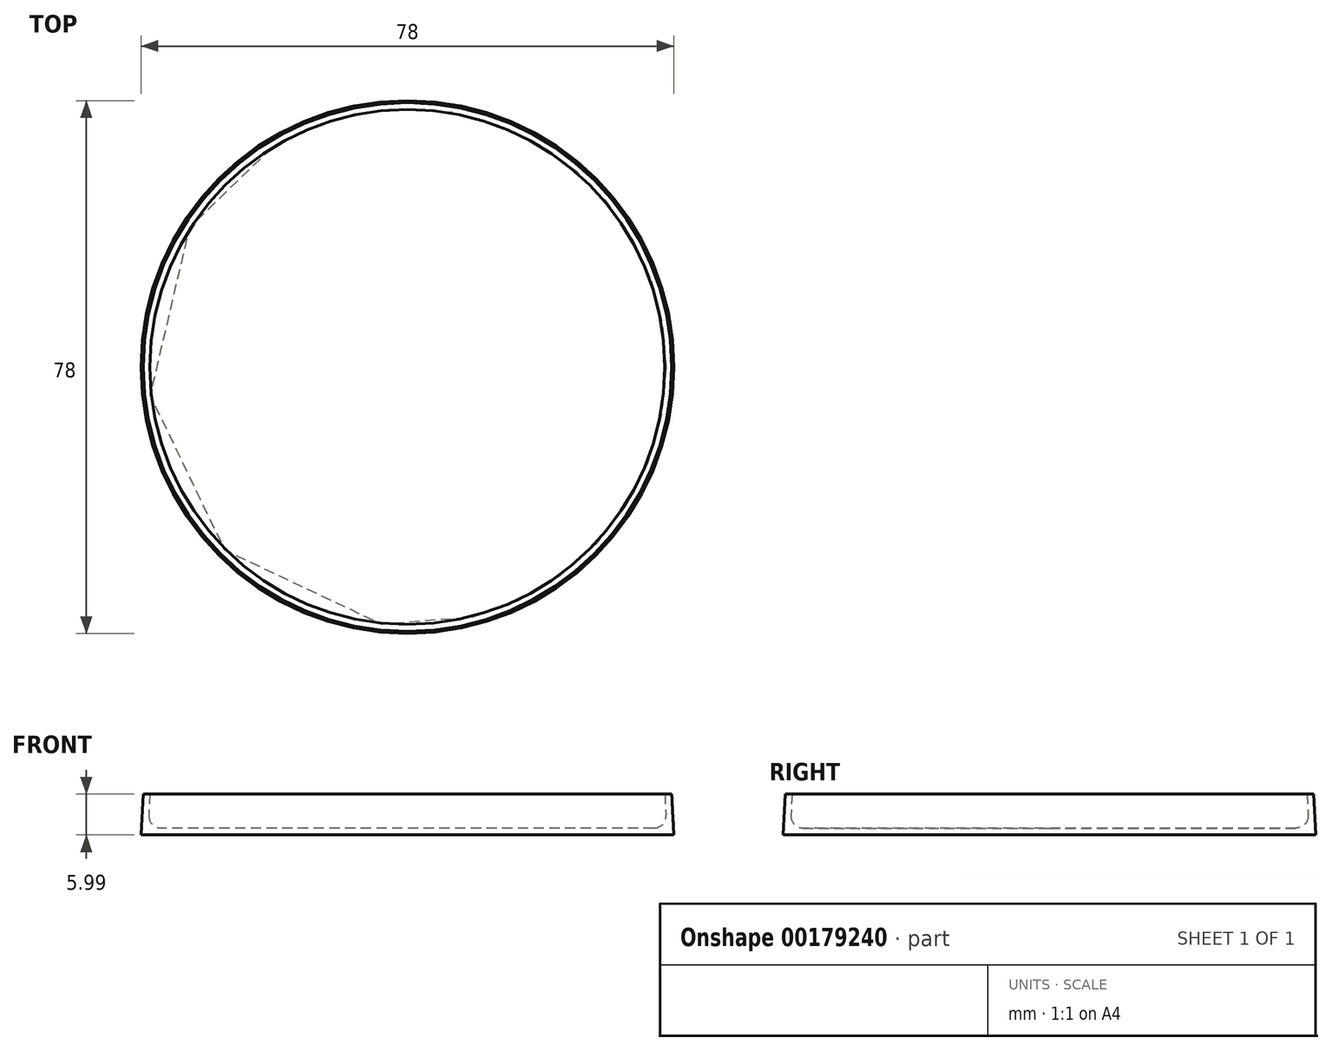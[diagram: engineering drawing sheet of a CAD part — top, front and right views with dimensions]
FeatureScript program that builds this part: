
annotation { "Feature Type Name" : "Feature", "Feature Type Description" : "" }
export const myFeature = defineFeature(function(context is Context, id is Id, definition is map)
    precondition{}
    {
        {
            var Q0;
            Q0=qCreatedBy(makeId("Front.planeOp"),FACE);
            var sketch = newSketch(context, id + "F0", { "sketchPlane" : qUnion([Q0])});
            skLineSegment(sketch, "E0", {"start": v(-39, 0) * mm, "end": v(-38.69, 6) * mm});
            skLineSegment(sketch, "E1", {"start": v(-38.69, 6) * mm, "end": v(-37.69, 6) * mm});
            skLineSegment(sketch, "E2", {"start": v(-37.69, 6) * mm, "end": v(-37.85, 2.87) * mm});
            skLineSegment(sketch, "E3", {"start": v(-36.07, 1) * mm, "end": v(0, 1) * mm});
            skLineSegment(sketch, "E4", {"start": v(0, 1) * mm, "end": v(0, 0) * mm});
            skLineSegment(sketch, "E5", {"start": v(0, 0) * mm, "end": v(-39, 0) * mm});
            skPoint(sketch, "E6.visualSharp", {"position": v(-37.95, 1) * mm});
            skArc(sketch, "E6.filletArc", {"start": v(-37.85, 2.87) * mm, "mid": v(-37.36, 1.55) * mm, "end": v(-36.07, 1) * mm});
            skSolve(sketch);
        }
        {
            var Q0;
            Q0=makeQuery(id+"F0.imprint","IMPRINT",FACE,{"disambiguationData":[TD([[makeQuery(id+"F0.imprint","IMPRINT",EDGE,{"derivedFrom":sQuery(id+"F0.wireOp",EDGE,"E0")}),-1.0]])]});
            var Q1;
            Q1=sQuery(id+"F0.wireOp",EDGE,"E4");
            revolve(context, id + "F1", {"entities" : qUnion([Q0]), "axis" : qUnion([Q1]), "revolveType" : RevolveType.FULL});
        }
    });
